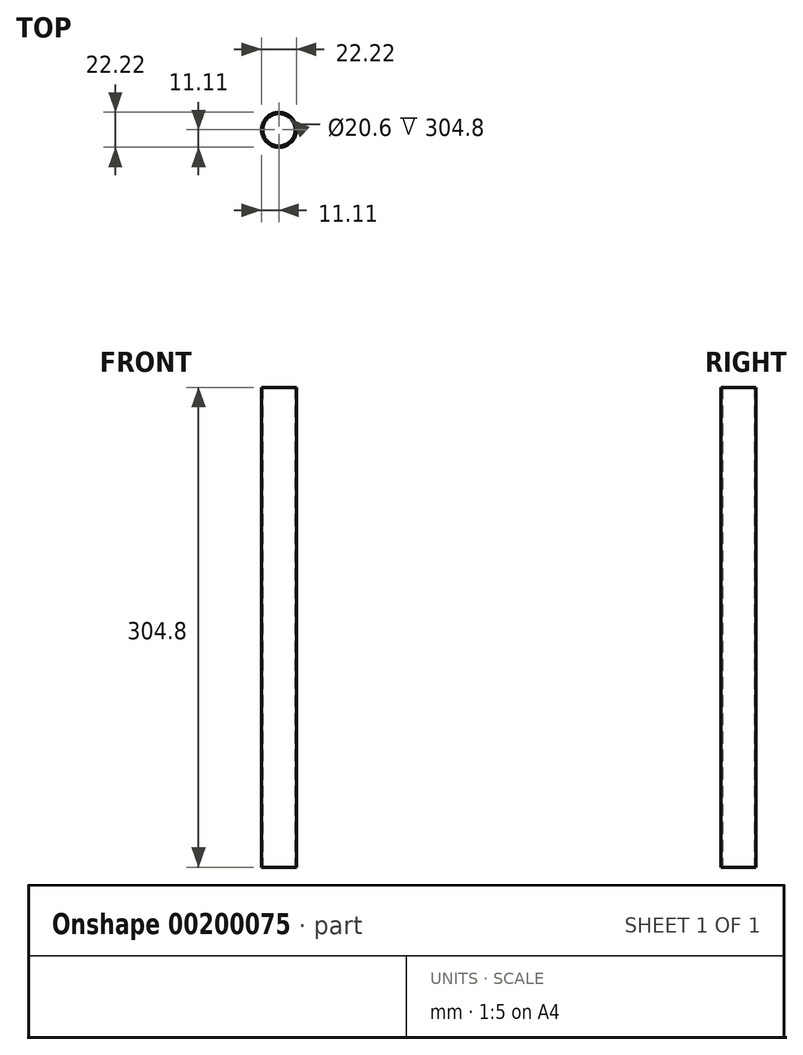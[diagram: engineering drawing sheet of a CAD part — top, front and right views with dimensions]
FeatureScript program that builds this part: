
annotation { "Feature Type Name" : "Feature", "Feature Type Description" : "" }
export const myFeature = defineFeature(function(context is Context, id is Id, definition is map)
    precondition{}
    {
        {
            var Q0;
            Q0=qCreatedBy(makeId("Top.planeOp"),FACE);
            var sketch = newSketch(context, id + "F0", { "sketchPlane" : qUnion([Q0])});
            skCircle(sketch, "E0", {"center": v(0, 0) * mm, "radius": 10.3 * mm});
            skCircle(sketch, "E1.0", {"center": v(0, 0) * mm, "radius": 11.11 * mm});
            skSolve(sketch);
        }
        {
            var Q0;
            Q0=makeQuery(id+"F0.imprint","IMPRINT",FACE,{"disambiguationData":[TD([[makeQuery(id+"F0.imprint","IMPRINT",EDGE,{"derivedFrom":sQuery(id+"F0.wireOp",EDGE,"E0")}),-1.0]])]});
            extrude(context, id + "F1", {"entities" : qUnion([Q0]), "depth" : 304.8 * mm});
        }
    });
